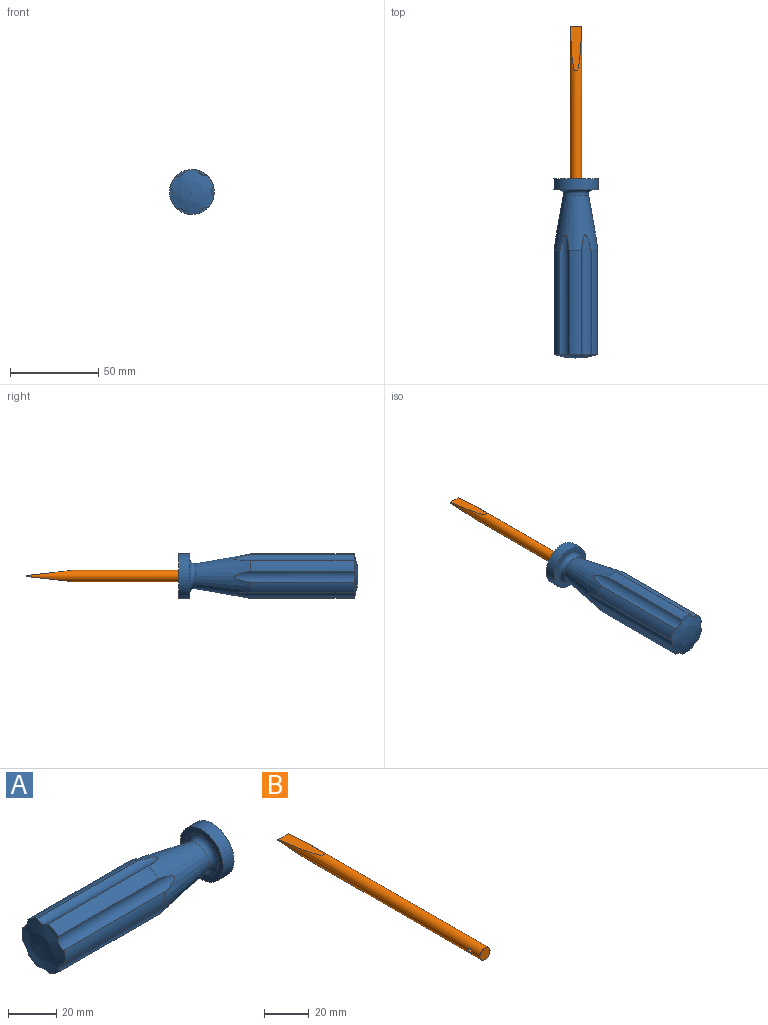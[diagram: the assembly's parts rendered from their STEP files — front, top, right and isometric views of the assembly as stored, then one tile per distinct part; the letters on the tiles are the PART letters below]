
ASSEMBLY  parts=2 mates=1
PART A: 20 faces, bbox 101.6x25.4x25.4 mm
  f0: cylinder r=12.7mm len=58.78mm, axis (-1,0,0), area 411.2mm2, adj f11,f13,f18,f19
  f1: cylinder r=12.7mm len=58.78mm, axis (-1,0,0), area 411.2mm2, adj f11,f13,f17,f18
  f2: cylinder r=12.7mm len=58.78mm, axis (-1,0,0), area 411.2mm2, adj f11,f13,f16,f17
  f3: cylinder r=12.7mm len=58.78mm, axis (-1,0,0), area 411.2mm2, adj f11,f13,f15,f16
  f4: cylinder r=12.7mm len=58.78mm, axis (-1,0,0), area 411.2mm2, adj f11,f13,f14,f15
  f5: plane 6.35x6.35mm, normal (1,0,0), area 31.7mm2, adj f6
  f6: cylinder r=3.17mm len=40.64mm, axis (-1,0,0), area 810.7mm2, adj f5,f7
  f7: plane 25.4x25.4mm, normal (1,0,0), area 475mm2, adj f6,f8
  f8: cylinder r=12.7mm len=25.4mm, axis (-1,0,0), area 506.7mm2, adj f7,f9
  f9: plane 25.4x25.4mm, normal (-1,0,0), area 212.3mm2, adj f8,f10
  f10: torus R=9.68mm, axis (-1,0,0), area 222.1mm2, adj f9,f11
  f11: cone r=7.18mm half-angle=10deg, axis (-1,0,0), area 1761.1mm2, adj f0,f1,f2,f3,f4,f10,f12,f14
  f12: cylinder r=12.7mm len=58.78mm, axis (-1,0,0), area 411.2mm2, adj f11,f13,f14,f19
  f13: sphere r=38.1mm, area 480.5mm2, adj f0,f1,f2,f3,f4,f12,f14,f15
  f14: cylinder r=4.83mm len=67.98mm, axis (1,0,0), area 439.5mm2, adj f4,f11,f12,f13
  f15: cylinder r=4.83mm len=67.98mm, axis (1,0,0), area 439.5mm2, adj f3,f4,f11,f13
  f16: cylinder r=4.83mm len=67.98mm, axis (1,0,0), area 439.5mm2, adj f2,f3,f11,f13
  f17: cylinder r=4.83mm len=67.98mm, axis (1,0,0), area 439.5mm2, adj f1,f2,f11,f13
  f18: cylinder r=4.83mm len=67.98mm, axis (1,0,0), area 439.5mm2, adj f0,f1,f11,f13
  f19: cylinder r=4.83mm len=67.98mm, axis (1,0,0), area 439.5mm2, adj f0,f11,f12,f13
PART B: 8 faces, bbox 6.4x127x6.4 mm
  f0: cylinder r=3.17mm len=127mm, axis (0,1,0), area 2206.6mm2, adj f1,f2,f3,f4,f5,f6,f7
  f1: plane 6.35x0.52mm, normal (0,1,0), area 3.3mm2, adj f0,f4,f6
  f2: plane 6.35x6.35mm, normal (0,-1,0), area 31.7mm2, adj f0
  f3: plane 1.72x0.12mm, normal (0,1,0), area 0.1mm2, adj f0,f4
  f4: plane 25.4x6.33mm, normal (0,0.11,0.99), area 128.4mm2, adj f0,f1,f3
  f5: plane 1.72x0.12mm, normal (0,1,0), area 0.1mm2, adj f0,f6
  f6: plane 25.4x6.33mm, normal (0,0.11,-0.99), area 128.4mm2, adj f0,f1,f5
  f7: cylinder r=1.19mm len=6.35mm, axis (1,0,0), area 45.9mm2, adj f0
PLACE A rot(axis=(0.58,0.58,0.58),120deg) t=(-16.94,-25.68,42.83)mm
PLACE B t=(-16.94,60.68,42.83)mm
MATE planar A.f0 <-> B.f0  axis (0,1,0) through (-16.94,-66.32,42.83)mm
